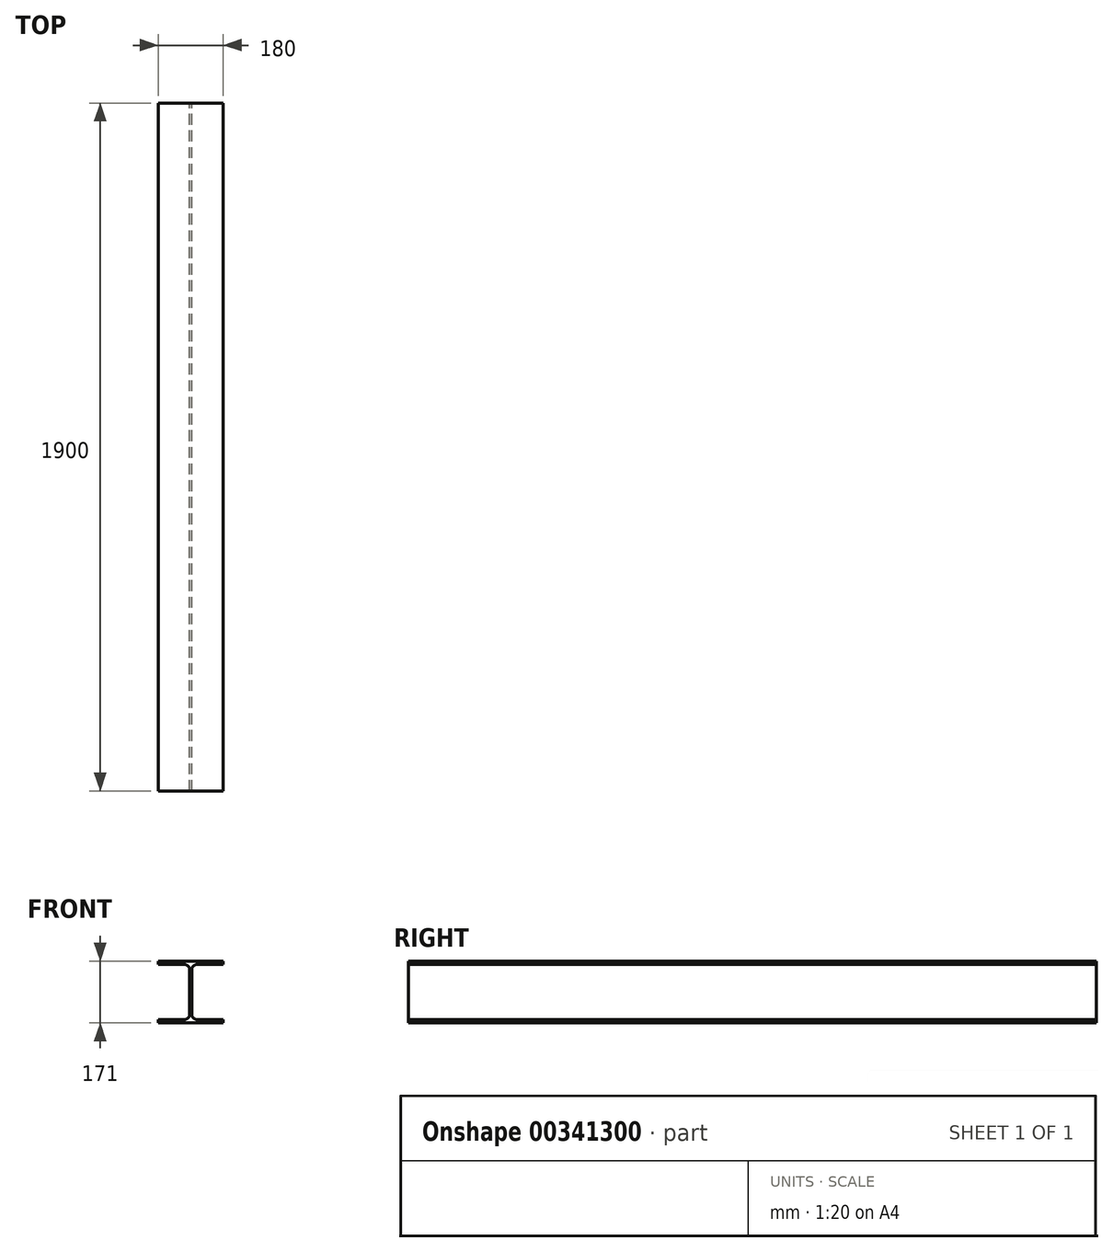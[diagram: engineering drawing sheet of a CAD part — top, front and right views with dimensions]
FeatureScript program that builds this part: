
annotation { "Feature Type Name" : "Feature", "Feature Type Description" : "" }
export const myFeature = defineFeature(function(context is Context, id is Id, definition is map)
    precondition{}
    {
        {
            var Q0;
            Q0=qCreatedBy(makeId("Front.planeOp"),FACE);
            var sketch = newSketch(context, id + "F0", { "sketchPlane" : qUnion([Q0])});
            skLineSegment(sketch, "E0", {"start": v(0, 0) * mm, "end": v(180, 0) * mm});
            skLineSegment(sketch, "E1", {"start": v(180, 0) * mm, "end": v(180, 9.5) * mm});
            skLineSegment(sketch, "E2", {"start": v(180, 9.5) * mm, "end": v(93, 9.5) * mm});
            skLineSegment(sketch, "E3", {"start": v(93, 9.5) * mm, "end": v(93, 161.5) * mm});
            skLineSegment(sketch, "E4", {"start": v(93, 161.5) * mm, "end": v(180, 161.5) * mm});
            skLineSegment(sketch, "E5", {"start": v(180, 161.5) * mm, "end": v(180, 171) * mm});
            skLineSegment(sketch, "E6", {"start": v(180, 171) * mm, "end": v(0, 171) * mm});
            skLineSegment(sketch, "E7", {"start": v(0, 171) * mm, "end": v(0, 161.5) * mm});
            skLineSegment(sketch, "E8", {"start": v(0, 161.5) * mm, "end": v(87, 161.5) * mm});
            skLineSegment(sketch, "E9", {"start": v(87, 161.5) * mm, "end": v(87, 9.5) * mm});
            skLineSegment(sketch, "E10", {"start": v(87, 9.5) * mm, "end": v(0, 9.5) * mm});
            skLineSegment(sketch, "E11", {"start": v(0, 9.5) * mm, "end": v(0, 0) * mm});
            skSolve(sketch);
        }
        {
            var Q0;
            Q0=makeQuery(id+"F0.imprint","IMPRINT",FACE,{"disambiguationData":[TD([[makeQuery(id+"F0.imprint","IMPRINT",EDGE,{"derivedFrom":sQuery(id+"F0.wireOp",EDGE,"E0")}),1.0]])]});
            extrude(context, id + "F1", {"entities" : qUnion([Q0]), "depth" : 1900 * mm});
        }
        {
            var Q0;
            Q0=makeQuery(id+"F1.opExtrude","SWEPT_EDGE",EDGE,{"disambiguationData":[OSD([sQuery(id+"F0.wireOp",EDGE,"E2"),sQuery(id+"F0.wireOp",EDGE,"E3")])]});
            var Q1;
            Q1=makeQuery(id+"F1.opExtrude","SWEPT_EDGE",EDGE,{"disambiguationData":[OSD([sQuery(id+"F0.wireOp",EDGE,"E3"),sQuery(id+"F0.wireOp",EDGE,"E4")])]});
            var Q2;
            Q2=makeQuery(id+"F1.opExtrude","SWEPT_EDGE",EDGE,{"disambiguationData":[OSD([sQuery(id+"F0.wireOp",EDGE,"E8"),sQuery(id+"F0.wireOp",EDGE,"E9")])]});
            var Q3;
            Q3=makeQuery(id+"F1.opExtrude","SWEPT_EDGE",EDGE,{"disambiguationData":[OSD([sQuery(id+"F0.wireOp",EDGE,"E9"),sQuery(id+"F0.wireOp",EDGE,"E10")])]});
            fillet(context, id + "F2", {"entities" : qUnion([Q0, Q1, Q2, Q3]), "radius" : 15 * mm, "tangentPropagation" : true, "allowEdgeOverflow" : false});
        }
    });
